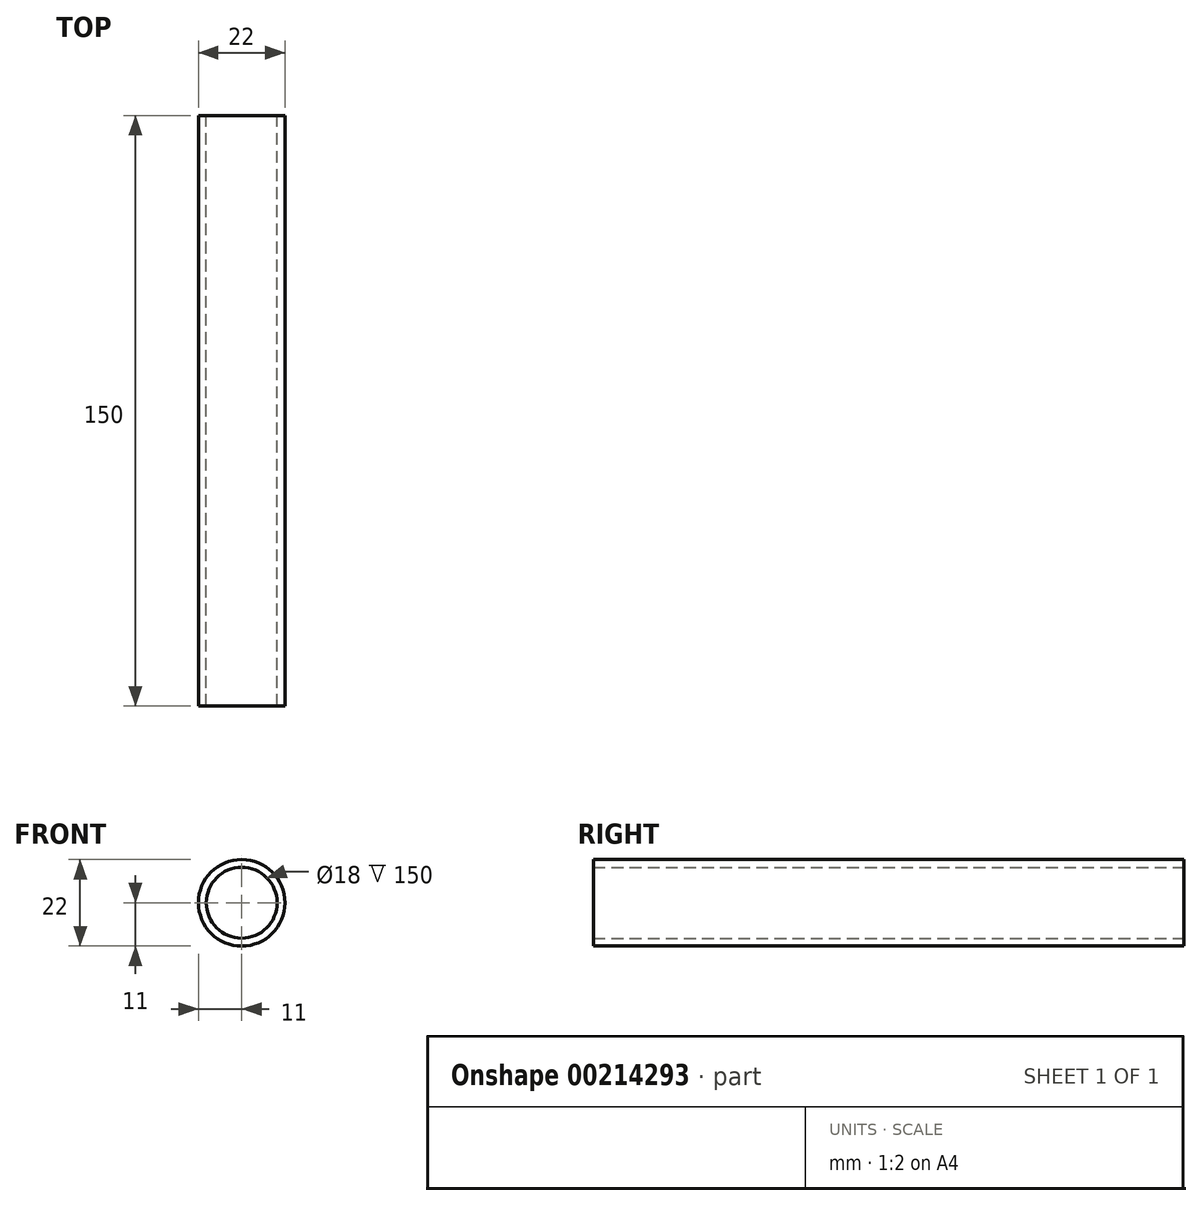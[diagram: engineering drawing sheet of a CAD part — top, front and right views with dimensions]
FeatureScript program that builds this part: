
annotation { "Feature Type Name" : "Feature", "Feature Type Description" : "" }
export const myFeature = defineFeature(function(context is Context, id is Id, definition is map)
    precondition{}
    {
        {
            var Q0;
            Q0=qCreatedBy(makeId("Front.planeOp"),FACE);
            var sketch = newSketch(context, id + "F0", { "sketchPlane" : qUnion([Q0])});
            skCircle(sketch, "E0", {"center": v(0, 0) * mm, "radius": 11 * mm});
            skCircle(sketch, "E1", {"center": v(0, 0) * mm, "radius": 9 * mm});
            skSolve(sketch);
        }
        {
            var Q0;
            Q0 = qSketchRegion(id + "F0", true);
            extrude(context, id + "F1", {"entities" : qUnion([Q0]), "depth" : 150 * mm});
        }
    });
